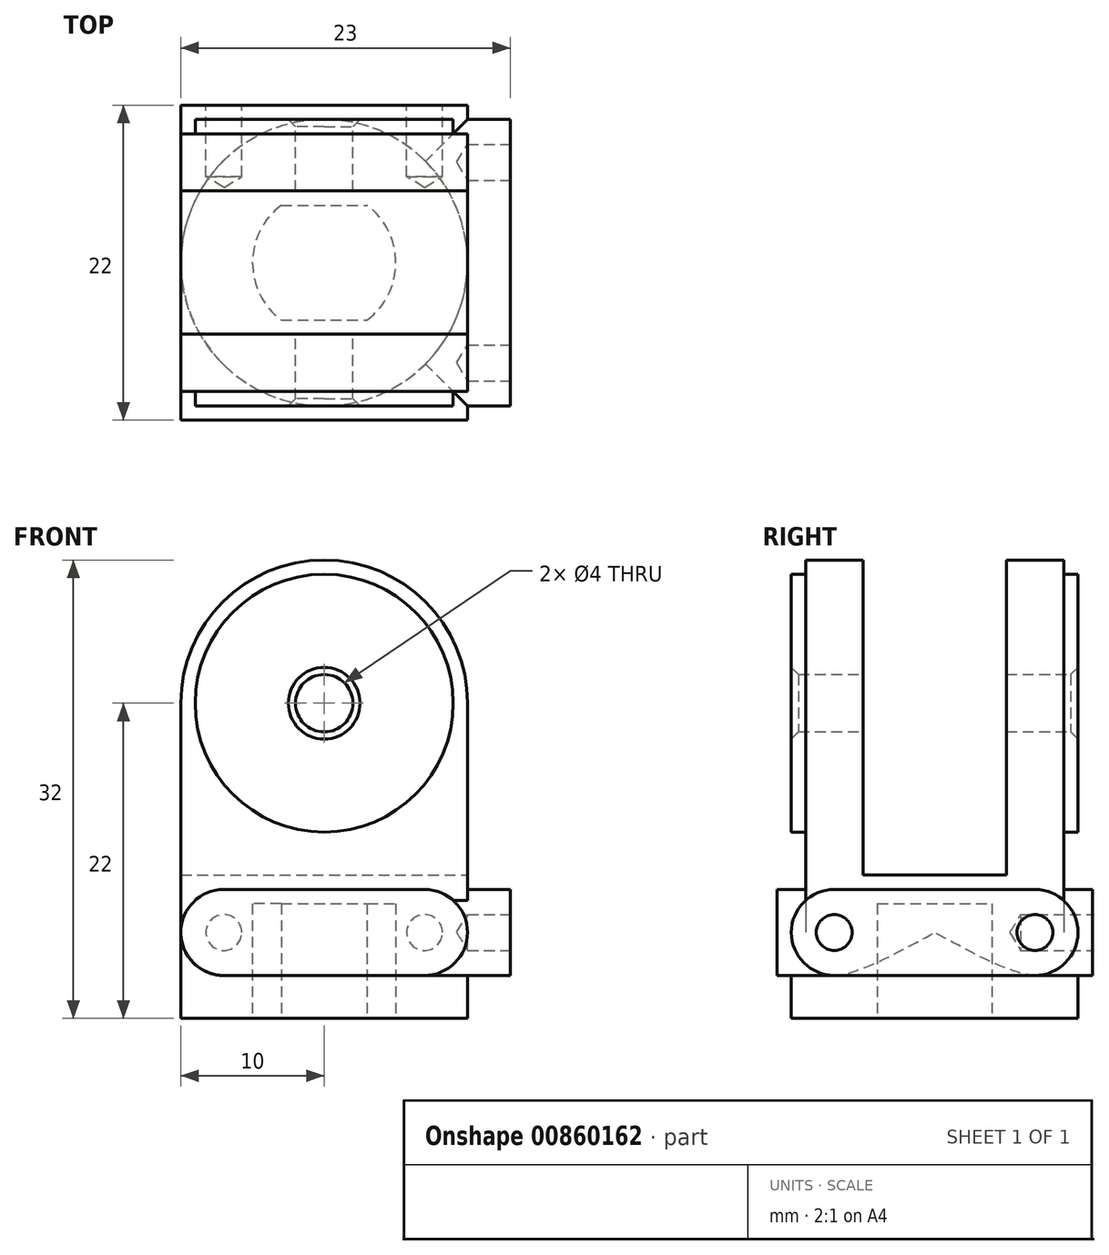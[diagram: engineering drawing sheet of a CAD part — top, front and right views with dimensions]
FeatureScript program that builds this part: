
annotation { "Feature Type Name" : "Feature", "Feature Type Description" : "" }
export const myFeature = defineFeature(function(context is Context, id is Id, definition is map)
    precondition{}
    {
        {
            var Q0;
            Q0=qCreatedBy(makeId("Top.planeOp"),FACE);
            cPlane(context, id + "F0", {"entities" : qUnion([Q0]), "cplaneType" : CPlaneType.OFFSET, "offset" : 22 * mm, "oppositeDirection" : true, "width" : 150 * mm, "height" : 150 * mm});
        }
        {
            var Q0;
            Q0=qCreatedBy(makeId("Front.planeOp"),FACE);
            var sketch = newSketch(context, id + "F1", { "sketchPlane" : qUnion([Q0])});
            skArc(sketch, "E0", {"start": v(10, 0) * mm, "mid": v(0, 10) * mm, "end": v(-10, 0) * mm});
            skLineSegment(sketch, "E1", {"start": v(-10, 0) * mm, "end": v(-10, -16) * mm});
            skLineSegment(sketch, "E2", {"start": v(10, 0) * mm, "end": v(10, -16) * mm});
            skLineSegment(sketch, "E3", {"start": v(-10, -16) * mm, "end": v(10, -16) * mm, "construction": true});
            skCircle(sketch, "E4", {"center": v(0, 0) * mm, "radius": 9 * mm});
            skArc(sketch, "E5", {"start": v(-7, -13) * mm, "mid": v(-10, -16) * mm, "end": v(-7, -19) * mm});
            skArc(sketch, "E6", {"start": v(7, -19) * mm, "mid": v(10, -16) * mm, "end": v(7, -13) * mm});
            skLineSegment(sketch, "E7", {"start": v(-7, -13) * mm, "end": v(7, -13) * mm});
            skLineSegment(sketch, "E8", {"start": v(-7, -19) * mm, "end": v(7, -19) * mm});
            skCircle(sketch, "E9", {"center": v(0, 0) * mm, "radius": 2 * mm});
            skSolve(sketch);
        }
        {
            var Q0;
            Q0 = qSketchRegion(id + "F1", true);
            var Q1;
            Q1=makeQuery(id+"F1.imprint","IMPRINT",FACE,{"disambiguationData":[TD([[makeQuery(id+"F1.imprint","IMPRINT",EDGE,{"derivedFrom":sQuery(id+"F1.wireOp",EDGE,"E4")}),1.0]])]});
            extrude(context, id + "F2", {"entities" : qUnion([Q0, Q1]), "endBound" : BoundingType.SYMMETRIC, "depth" : 18 * mm, "offsetDistance" : 25 * mm});
        }
        {
            var Q0;
            Q0=makeQuery(id+"F1.imprint","IMPRINT",FACE,{"disambiguationData":[TD([[makeQuery(id+"F1.imprint","IMPRINT",EDGE,{"derivedFrom":sQuery(id+"F1.wireOp",EDGE,"E4")}),1.0]])]});
            extrude(context, id + "F3", {"entities" : qUnion([Q0]), "operationType" : NewBodyOperationType.ADD, "endBound" : BoundingType.SYMMETRIC, "depth" : 20 * mm, "offsetDistance" : 25 * mm});
        }
        {
            var Q0;
            Q0=makeQuery(id+"F3.opExtrude","CAP_EDGE",EDGE,{"disambiguationData":[OSD([sQuery(id+"F1.wireOp",EDGE,"E9")])],"isStart":true});
            var Q1;
            Q1=makeQuery(id+"F3.opExtrude","CAP_EDGE",EDGE,{"disambiguationData":[OSD([sQuery(id+"F1.wireOp",EDGE,"E9")])],"isStart":false});
            chamfer(context, id + "F4", {"entities" : qUnion([Q0, Q1]), "width" : 0.5 * mm, "tangentPropagation" : true});
        }
        {
            var Q0;
            {var subQ2=sQuery(id+"F1.wireOp",EDGE,"E7");Q0=makeQuery(id+"F1.imprint","IMPRINT",FACE,{"disambiguationData":[TD([[makeQuery(id+"F1.imprint","IMPRINT",EDGE,{"derivedFrom":subQ2}),-1.0]])]});}
            extrude(context, id + "F5", {"entities" : qUnion([Q0]), "operationType" : NewBodyOperationType.ADD, "endBound" : BoundingType.SYMMETRIC, "depth" : 22 * mm, "offsetDistance" : 25 * mm});
        }
        {
            var Q0;
            Q0=qCreatedBy(makeId("Right.planeOp"),FACE);
            var sketch = newSketch(context, id + "F6", { "sketchPlane" : qUnion([Q0])});
            skLineSegment(sketch, "E10", {"start": v(0, -9) * mm, "end": v(0, -13) * mm, "construction": true});
            skLineSegment(sketch, "E11", {"start": v(0, 10) * mm, "end": v(0, 9) * mm, "construction": true});
            skLineSegment(sketch, "E12.bottom", {"start": v(-5, -12) * mm, "end": v(5, -12) * mm});
            skLineSegment(sketch, "E12.top", {"start": v(-5, 10) * mm, "end": v(5, 10) * mm});
            skLineSegment(sketch, "E12.left", {"start": v(-5, -12) * mm, "end": v(-5, 10) * mm});
            skLineSegment(sketch, "E12.right", {"start": v(5, -12) * mm, "end": v(5, 10) * mm});
            skPoint(sketch, "E12.middle", {"position": v(0, -1) * mm});
            skSolve(sketch);
        }
        {
            var Q0;
            Q0 = qSketchRegion(id + "F6", true);
            extrude(context, id + "F7", {"entities" : qUnion([Q0]), "operationType" : NewBodyOperationType.REMOVE, "endBound" : BoundingType.SYMMETRIC, "oppositeDirection" : true, "depth" : 25 * mm, "offsetDistance" : 25 * mm});
        }
        {
            var Q0;
            Q0=qCreatedBy(id+"F0.planeOp",FACE);
            var sketch = newSketch(context, id + "F8", { "sketchPlane" : qUnion([Q0])});
            skCircle(sketch, "E13", {"center": v(0, 0) * mm, "radius": 10 * mm});
            skPoint(sketch, "E14.0", {"position": v(-10, 0) * mm});
            skSolve(sketch);
        }
        {
            var Q0;
            Q0=qCreatedBy(makeId("Right.planeOp"),FACE);
            var sketch = newSketch(context, id + "F9", { "sketchPlane" : qUnion([Q0])});
            skLineSegment(sketch, "E15", {"start": v(-7, -16) * mm, "end": v(7, -16) * mm, "construction": true});
            skArc(sketch, "E16.0.startCap", {"start": v(-7, -19) * mm, "mid": v(-10, -16) * mm, "end": v(-7, -13) * mm});
            skArc(sketch, "E16.0.endCap", {"start": v(7, -13) * mm, "mid": v(10, -16) * mm, "end": v(7, -19) * mm});
            skLineSegment(sketch, "E16.0.left", {"start": v(-7, -13) * mm, "end": v(7, -13) * mm});
            skLineSegment(sketch, "E16.0.right", {"start": v(-7, -19) * mm, "end": v(7, -19) * mm});
            skSolve(sketch);
        }
        {
            var Q0;
            Q0 = qSketchRegion(id + "F9", true);
            extrude(context, id + "F10", {"entities" : qUnion([Q0]), "operationType" : NewBodyOperationType.ADD, "depth" : 13 * mm, "offsetDistance" : 25 * mm});
        }
        {
            var Q0;
            Q0 = qSketchRegion(id + "F8", true);
            var Q1;
            {var subQ0=sQuery(id+"F1.wireOp",EDGE,"E8");Q1=makeQuery(id+"F10.boolean.opBoolean","MERGE",FACE,{"derivedFrom":[makeQuery(id+"F5.boolean.opBoolean","MERGE",FACE,{"derivedFrom":[makeQuery(id+"F2.opExtrude","SWEPT_FACE",FACE,{"disambiguationData":[OSD([subQ0])]}),makeQuery(id+"F5.opExtrude","SWEPT_FACE",FACE,{"disambiguationData":[OSD([subQ0])]})]}),makeQuery(id+"F10.opExtrude","SWEPT_FACE",FACE,{"disambiguationData":[OSD([sQuery(id+"F9.wireOp",EDGE,"E16.0.right")])]})]});}
            var Q2;
            Q2=makeQuery(id+"F2.opExtrude","SWEPT_BODY",BODY,{"disambiguationData":[OSD([sQuery(id+"F1.wireOp",EDGE,"E0"),sQuery(id+"F1.wireOp",EDGE,"E1"),sQuery(id+"F1.wireOp",EDGE,"E2"),sQuery(id+"F1.wireOp",EDGE,"E5"),sQuery(id+"F1.wireOp",EDGE,"E6"),sQuery(id+"F1.wireOp",EDGE,"E8"),sQuery(id+"F1.wireOp",EDGE,"E9")])]});
            extrude(context, id + "F11", {"entities" : qUnion([Q0]), "operationType" : NewBodyOperationType.ADD, "endBound" : BoundingType.UP_TO_NEXT, "depth" : 25 * mm, "endBoundEntityFace" : qUnion([Q1]), "endBoundEntityBody" : qUnion([Q2]), "offsetDistance" : 25 * mm});
        }
        {
            var Q0;
            Q0=makeQuery(id+"F5.opExtrude","CAP_FACE",FACE,{"disambiguationData":[OSD([sQuery(id+"F1.wireOp",EDGE,"E5"),sQuery(id+"F1.wireOp",EDGE,"E6"),sQuery(id+"F1.wireOp",EDGE,"E7"),sQuery(id+"F1.wireOp",EDGE,"E8")])],"isStart":true});
            var sketch = newSketch(context, id + "F12", { "sketchPlane" : qUnion([Q0])});
            skPoint(sketch, "E17", {"position": v(-7, -16) * mm});
            skPoint(sketch, "E18", {"position": v(7, -16) * mm});
            skSolve(sketch);
        }
        {
            var Q0;
            Q0=sQuery(id+"F12.wireOp",VERTEX,"E17");
            var Q1;
            Q1=sQuery(id+"F12.wireOp",VERTEX,"E18");
            var Q2;
            Q2=makeQuery(id+"F2.opExtrude","SWEPT_BODY",BODY,{"disambiguationData":[OSD([sQuery(id+"F1.wireOp",EDGE,"E0"),sQuery(id+"F1.wireOp",EDGE,"E1"),sQuery(id+"F1.wireOp",EDGE,"E2"),sQuery(id+"F1.wireOp",EDGE,"E5"),sQuery(id+"F1.wireOp",EDGE,"E6"),sQuery(id+"F1.wireOp",EDGE,"E8"),sQuery(id+"F1.wireOp",EDGE,"E9")])]});
            hole(context, id + "F13", {"style" : HoleStyle.SIMPLE, "endStyle" : HoleEndStyle.BLIND, "standardTappedOrClearance" : lookupTablePath({ "standard" : "ISO", "engagement" : "75%", "pitch" : "0.5 mm", "size" : "M3", "type" : "Tapped" }), "standardBlindInLast" : lookupTablePath({ "standard" : "ISO", "engagement" : "75%", "pitch" : "0.5 mm", "size" : "M3", "type" : "Tapped" }), "holeDiameter" : 2.5 * mm, "majorDiameter" : 3 * mm, "showTappedDepth" : true, "holeDepth" : 5 * mm, "isTappedThrough" : true, "tappedDepth" : 5 * mm, "tapClearance" : 0, "startFromSketch" : true, "locations" : qUnion([Q0, Q1]), "scope" : qUnion([Q2])});
        }
        {
            var Q0;
            Q0=makeQuery(id+"F10.opExtrude","CAP_FACE",FACE,{"disambiguationData":[OSD([sQuery(id+"F9.wireOp",EDGE,"E16.0.startCap"),sQuery(id+"F9.wireOp",EDGE,"E16.0.endCap"),sQuery(id+"F9.wireOp",EDGE,"E16.0.left"),sQuery(id+"F9.wireOp",EDGE,"E16.0.right")])],"isStart":false});
            var sketch = newSketch(context, id + "F14", { "sketchPlane" : qUnion([Q0])});
            skPoint(sketch, "E19", {"position": v(-7, -16) * mm});
            skPoint(sketch, "E20", {"position": v(7, -16) * mm});
            skSolve(sketch);
        }
        {
            var Q0;
            Q0=sQuery(id+"F14.wireOp",VERTEX,"E19");
            var Q1;
            Q1=sQuery(id+"F14.wireOp",VERTEX,"E20");
            var Q2;
            Q2=makeQuery(id+"F2.opExtrude","SWEPT_BODY",BODY,{"disambiguationData":[OSD([sQuery(id+"F1.wireOp",EDGE,"E0"),sQuery(id+"F1.wireOp",EDGE,"E1"),sQuery(id+"F1.wireOp",EDGE,"E2"),sQuery(id+"F1.wireOp",EDGE,"E5"),sQuery(id+"F1.wireOp",EDGE,"E6"),sQuery(id+"F1.wireOp",EDGE,"E8"),sQuery(id+"F1.wireOp",EDGE,"E9")])]});
            hole(context, id + "F15", {"style" : HoleStyle.SIMPLE, "endStyle" : HoleEndStyle.BLIND, "standardTappedOrClearance" : lookupTablePath({ "standard" : "ISO", "engagement" : "75%", "pitch" : "0.5 mm", "size" : "M3", "type" : "Tapped" }), "standardBlindInLast" : lookupTablePath({ "standard" : "ISO", "engagement" : "75%", "pitch" : "0.5 mm", "size" : "M3", "type" : "Tapped" }), "holeDiameter" : 2.5 * mm, "majorDiameter" : 3 * mm, "showTappedDepth" : true, "holeDepth" : 3 * mm, "isTappedThrough" : true, "tappedDepth" : 3 * mm, "tapClearance" : 0, "startFromSketch" : true, "locations" : qUnion([Q0, Q1]), "scope" : qUnion([Q2])});
        }
        {
            var Q0;
            Q0=qCreatedBy(id+"F0.planeOp",FACE);
            var sketch = newSketch(context, id + "F16", { "sketchPlane" : qUnion([Q0])});
            skArc(sketch, "E21", {"start": v(3, -4) * mm, "mid": v(5, 0) * mm, "end": v(3, 4) * mm});
            skLineSegment(sketch, "E22", {"start": v(-3, -4) * mm, "end": v(3, -4) * mm});
            skLineSegment(sketch, "E23", {"start": v(-3, 4) * mm, "end": v(3, 4) * mm});
            skArc(sketch, "E24.trimOffspring", {"start": v(-3, 4) * mm, "mid": v(-5, 0) * mm, "end": v(-3, -4) * mm});
            skSolve(sketch);
        }
        {
            var Q0;
            Q0 = qSketchRegion(id + "F16", true);
            extrude(context, id + "F17", {"entities" : qUnion([Q0]), "operationType" : NewBodyOperationType.REMOVE, "depth" : 8 * mm, "offsetDistance" : 25 * mm});
        }
    });
